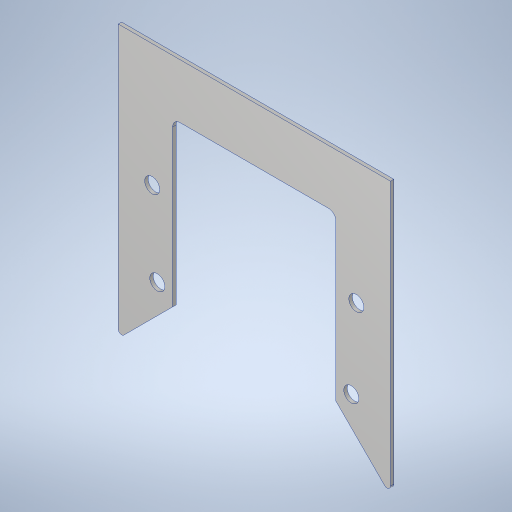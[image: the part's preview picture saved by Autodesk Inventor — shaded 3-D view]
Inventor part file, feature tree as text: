
AUTODESK INVENTOR PART (.ipt)
format: ipt  version: 2023.4 (Build 274418000, 418)  size: 264,192 bytes
history: native  units: in
note: dims shown in document units (in); Inventor stores cm internally (conversion verified against a paired STEP export)
features: fillet x2, sketch x2, extrude x1, hole x1
ambient origin geometry x8: Origin, YZ Plane, XZ Plane, XY Plane, X Axis, Y Axis, Z Axis, Center Point
bodies: Solid1 (feature_tree)
feature tree (6):
  extrude  "Extrusion1"  Depth=4.0in
  hole  "Hole1"  [1 undecoded]
  fillet  "Fillet1"  Radius=1.5in
  fillet  "Fillet2"  Radius=1.5in
  sketch  "Sketch1"  dims[d2=4.0in d3=4.0in]
  sketch  "Sketch2"  dims[d4=0.25in d5=0.0in d6=1.125in d7=1.5in d8=1.5in d9=1.125in d10=1.1in d11=0.75in d12=0.507in d13=0.25in d14=0.5635in d15=1.0in d16=0.8108in d18=6.004in d20=6.004in d21=4.0in d23=12.0in d25=5.0in d26=0.55in d27=0.25in]
note: 1 required parameter value undecoded (feature->parameter linkage not recoverable at this tier; creation-order binding heuristic only, values carry confidence <= 0.55)
